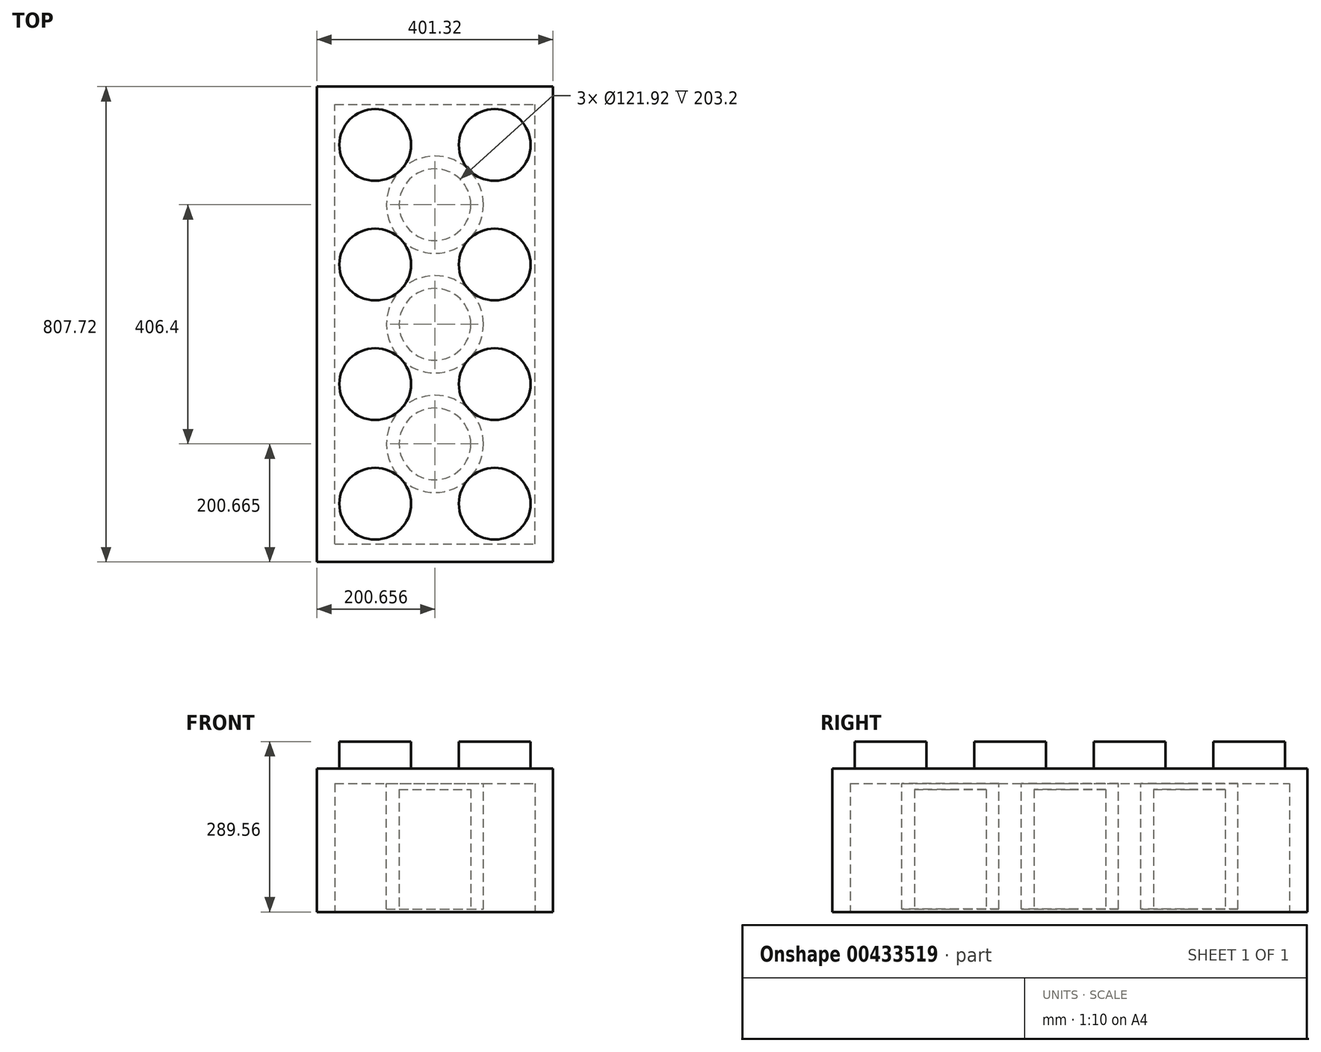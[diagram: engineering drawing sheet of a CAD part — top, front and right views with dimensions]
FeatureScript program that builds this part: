
annotation { "Feature Type Name" : "Feature", "Feature Type Description" : "" }
export const myFeature = defineFeature(function(context is Context, id is Id, definition is map)
    precondition{}
    {
        {
            var Q0;
            Q0=qCreatedBy(makeId("Top.planeOp"),FACE);
            var sketch = newSketch(context, id + "F0", { "sketchPlane" : qUnion([Q0])});
            skLineSegment(sketch, "E0.bottom", {"start": v(-168.28, 778.9) * mm, "end": v(233.04, 778.9) * mm});
            skLineSegment(sketch, "E0.top", {"start": v(-168.28, -28.82) * mm, "end": v(233.04, -28.82) * mm});
            skLineSegment(sketch, "E0.left", {"start": v(-168.28, 778.9) * mm, "end": v(-168.28, -28.82) * mm});
            skLineSegment(sketch, "E0.right", {"start": v(233.04, 778.9) * mm, "end": v(233.04, -28.82) * mm});
            skSolve(sketch);
        }
        {
            var Q0;
            Q0=makeQuery(id+"F0.imprint","IMPRINT",FACE,{"disambiguationData":[TD([[makeQuery(id+"F0.imprint","IMPRINT",EDGE,{"derivedFrom":sQuery(id+"F0.wireOp",EDGE,"E0.bottom")}),-1.0]])]});
            extrude(context, id + "F1", {"entities" : qUnion([Q0]), "depth" : 243.84 * mm});
        }
        {
            var Q0;
            Q0=makeQuery(id+"F1.opExtrude","CAP_FACE",FACE,{"disambiguationData":[OSD([sQuery(id+"F0.wireOp",EDGE,"E0.bottom"),sQuery(id+"F0.wireOp",EDGE,"E0.top"),sQuery(id+"F0.wireOp",EDGE,"E0.left"),sQuery(id+"F0.wireOp",EDGE,"E0.right")])],"isStart":false});
            var sketch = newSketch(context, id + "F2", { "sketchPlane" : qUnion([Q0])});
            skCircle(sketch, "E1", {"center": v(-69.22, 70.24) * mm, "radius": 60.96 * mm});
            skCircle(sketch, "E2.0.1.0", {"center": v(-69.22, 273.44) * mm, "radius": 60.96 * mm});
            skCircle(sketch, "E2.0.2.0", {"center": v(-69.22, 476.64) * mm, "radius": 60.96 * mm});
            skCircle(sketch, "E2.0.3.0", {"center": v(-69.22, 679.84) * mm, "radius": 60.96 * mm});
            skCircle(sketch, "E2.1.0.0", {"center": v(133.98, 70.24) * mm, "radius": 60.96 * mm});
            skCircle(sketch, "E2.1.1.0", {"center": v(133.98, 273.44) * mm, "radius": 60.96 * mm});
            skCircle(sketch, "E2.1.2.0", {"center": v(133.98, 476.64) * mm, "radius": 60.96 * mm});
            skCircle(sketch, "E2.1.3.0", {"center": v(133.98, 679.84) * mm, "radius": 60.96 * mm});
            skLineSegment(sketch, "E2.direction1", {"start": v(-69.22, 70.24) * mm, "end": v(133.98, 70.24) * mm, "construction": true});
            skLineSegment(sketch, "E2.direction2", {"start": v(-69.22, 70.24) * mm, "end": v(-69.22, 273.44) * mm, "construction": true});
            skSolve(sketch);
        }
        {
            var Q0;
            Q0 = qSketchRegion(id + "F2", true);
            extrude(context, id + "F3", {"entities" : qUnion([Q0]), "operationType" : NewBodyOperationType.ADD, "depth" : 45.72 * mm});
        }
        {
            var Q0;
            Q0=makeQuery(id+"F1.opExtrude","CAP_FACE",FACE,{"disambiguationData":[OSD([sQuery(id+"F0.wireOp",EDGE,"E0.bottom"),sQuery(id+"F0.wireOp",EDGE,"E0.top"),sQuery(id+"F0.wireOp",EDGE,"E0.left"),sQuery(id+"F0.wireOp",EDGE,"E0.right")])],"isStart":true});
            var sketch = newSketch(context, id + "F4", { "sketchPlane" : qUnion([Q0])});
            skLineSegment(sketch, "E3.bottom", {"start": v(-137.8, -1.66) * mm, "end": v(202.56, -1.66) * mm});
            skLineSegment(sketch, "E3.top", {"start": v(-137.8, -748.42) * mm, "end": v(202.56, -748.42) * mm});
            skLineSegment(sketch, "E3.left", {"start": v(-137.8, -1.66) * mm, "end": v(-137.8, -748.42) * mm});
            skLineSegment(sketch, "E3.right", {"start": v(202.56, -1.66) * mm, "end": v(202.56, -748.42) * mm});
            skSolve(sketch);
        }
        {
            var Q0;
            Q0 = qSketchRegion(id + "F4", true);
            extrude(context, id + "F5", {"entities" : qUnion([Q0]), "operationType" : NewBodyOperationType.REMOVE, "oppositeDirection" : true, "depth" : 218.44 * mm});
        }
        {
            var Q0;
            Q0=makeQuery(id+"F5.boolean.opBoolean","COPY",FACE,{"derivedFrom":makeQuery(id+"F5.opExtrude","CAP_FACE",FACE,{"disambiguationData":[OSD([sQuery(id+"F4.wireOp",EDGE,"E3.bottom"),sQuery(id+"F4.wireOp",EDGE,"E3.top"),sQuery(id+"F4.wireOp",EDGE,"E3.left"),sQuery(id+"F4.wireOp",EDGE,"E3.right")])],"isStart":false})});
            var sketch = newSketch(context, id + "F6", { "sketchPlane" : qUnion([Q0])});
            skCircle(sketch, "E4", {"center": v(32.38, -578.24) * mm, "radius": 82.55 * mm});
            skCircle(sketch, "E5.0.1.0", {"center": v(32.38, -375.04) * mm, "radius": 82.55 * mm});
            skCircle(sketch, "E5.0.2.0", {"center": v(32.38, -171.84) * mm, "radius": 82.55 * mm});
            skLineSegment(sketch, "E5.direction1", {"start": v(32.38, -578.24) * mm, "end": v(57.78, -578.24) * mm, "construction": true});
            skLineSegment(sketch, "E5.direction2", {"start": v(32.38, -578.24) * mm, "end": v(32.38, -375.04) * mm, "construction": true});
            skSolve(sketch);
        }
        {
            var Q0;
            Q0 = qSketchRegion(id + "F6", true);
            extrude(context, id + "F7", {"entities" : qUnion([Q0]), "operationType" : NewBodyOperationType.ADD, "depth" : 213.36 * mm});
        }
        {
            var Q0;
            Q0=makeQuery(id+"F7.opExtrude","CAP_FACE",FACE,{"disambiguationData":[OSD([sQuery(id+"F6.wireOp",EDGE,"E5.0.2.0")])],"isStart":false});
            var sketch = newSketch(context, id + "F8", { "sketchPlane" : qUnion([Q0])});
            skCircle(sketch, "E6", {"center": v(32.38, -171.84) * mm, "radius": 60.96 * mm});
            skCircle(sketch, "E7.0.1.0", {"center": v(32.38, -375.04) * mm, "radius": 60.96 * mm});
            skCircle(sketch, "E7.0.2.0", {"center": v(32.38, -578.24) * mm, "radius": 60.96 * mm});
            skLineSegment(sketch, "E7.direction1", {"start": v(32.38, -171.84) * mm, "end": v(57.78, -171.84) * mm, "construction": true});
            skLineSegment(sketch, "E7.direction2", {"start": v(32.38, -171.84) * mm, "end": v(32.38, -375.04) * mm, "construction": true});
            skSolve(sketch);
        }
        {
            var Q0;
            Q0 = qSketchRegion(id + "F8", true);
            extrude(context, id + "F9", {"entities" : qUnion([Q0]), "operationType" : NewBodyOperationType.REMOVE, "oppositeDirection" : true, "depth" : 203.2 * mm});
        }
    });
